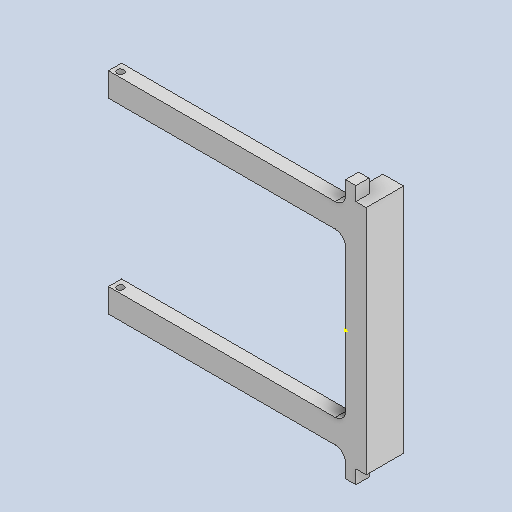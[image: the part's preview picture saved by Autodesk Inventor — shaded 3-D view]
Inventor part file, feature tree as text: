
AUTODESK INVENTOR PART (.ipt)
format: ipt  version: 2022 (Build 260153000, 153)  size: 193,536 bytes
history: native  units: mm
features: sketch x6, extrude x5, projected_geometry x4, other x3, reference x2, fillet x1
ambient origin geometry x8: Origin, YZ Plane, XZ Plane, XY Plane, X Axis, Y Axis, Z Axis, Center Point
bodies: Body1 (feature_tree)
feature tree (21):
  extrude  "Выдавливание8"  Depth=3.0mm
  extrude  "Выдавливание9"  Depth=0.3mm
  fillet  "Сопряжение9"  Radius=0.3mm
  extrude  "Выдавливание10"  Depth=0.3mm
  sketch  "Эскиз11"
  extrude  "Выдавливание11"  Depth=0.3mm
  extrude  "Выдавливание12"  Depth=6.7mm
  sketch  "Эскиз8"
  reference  "Ссылка14"
  sketch  "Эскиз9"
  projected_geometry  "Спроецированная петля2"
  sketch  "Эскиз10"
  reference  "Ссылка17"
  sketch  "Эскиз12"
  projected_geometry  "Спроецированная петля3"
  projected_geometry  "Спроецированная петля4"
  sketch  "Эскиз13"
  projected_geometry  "Спроецированная петля5"
  other  "<userpath>\Documents\Git\MZCAT_2024_construction\MZCAT_2024_RPI_2\MZCAT_4.iam"
  other  "MZCAT_4.iam"
  other  "motherboard_plate:1"
